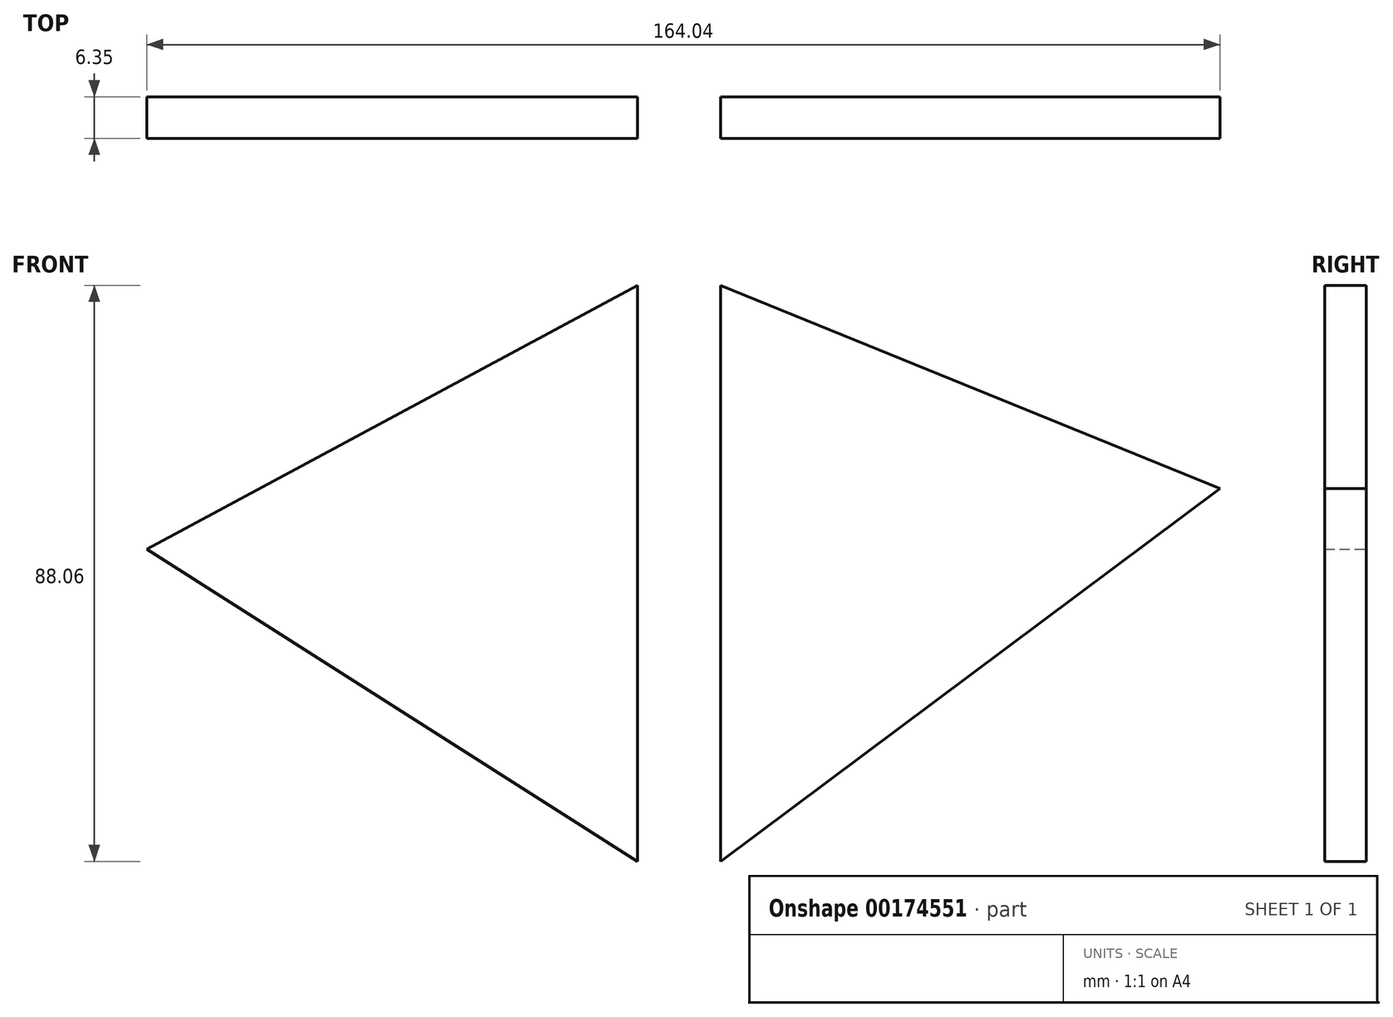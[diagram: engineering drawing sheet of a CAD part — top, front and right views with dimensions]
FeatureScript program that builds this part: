
annotation { "Feature Type Name" : "Feature", "Feature Type Description" : "" }
export const myFeature = defineFeature(function(context is Context, id is Id, definition is map)
    precondition{}
    {
        {
            var Q0;
            Q0=qCreatedBy(makeId("Front.planeOp"),FACE);
            var sketch = newSketch(context, id + "F0", { "sketchPlane" : qUnion([Q0])});
            skLineSegment(sketch, "E0", {"start": v(-12.7, 88.06) * mm, "end": v(-12.7, 0) * mm});
            skLineSegment(sketch, "E1", {"start": v(-12.7, 0) * mm, "end": v(-87.72, 47.7) * mm});
            skLineSegment(sketch, "E2", {"start": v(-87.72, 47.7) * mm, "end": v(-12.7, 88.06) * mm});
            skLineSegment(sketch, "E3", {"start": v(0, 88.06) * mm, "end": v(0, 0) * mm});
            skLineSegment(sketch, "E4", {"start": v(0, 0) * mm, "end": v(76.32, 57) * mm});
            skLineSegment(sketch, "E5", {"start": v(76.32, 57) * mm, "end": v(0, 88.06) * mm});
            skSolve(sketch);
        }
        {
            var Q0;
            Q0=qCreatedBy(makeId("Front.planeOp"),FACE);
            var sketch = newSketch(context, id + "F1", { "sketchPlane" : qUnion([Q0])});
            skLineSegment(sketch, "E6.0", {"start": v(-87.72, 47.7) * mm, "end": v(-12.7, 88.06) * mm});
            skLineSegment(sketch, "E7.0", {"start": v(-12.7, 0) * mm, "end": v(-87.72, 47.7) * mm});
            skLineSegment(sketch, "E8.0", {"start": v(-12.7, 88.06) * mm, "end": v(-12.7, 0) * mm});
            skLineSegment(sketch, "E9.0.0", {"start": v(76.32, 57) * mm, "end": v(0, 88.06) * mm});
            skLineSegment(sketch, "E9.0.1", {"start": v(0, 88.06) * mm, "end": v(0, 0) * mm});
            skLineSegment(sketch, "E9.0.2", {"start": v(0, 0) * mm, "end": v(76.32, 57) * mm});
            skSolve(sketch);
        }
        {
            var Q0;
            Q0 = qSketchRegion(id + "F1", true);
            extrude(context, id + "F2", {"entities" : qUnion([Q0]), "depth" : 6.35 * mm});
        }
    });
